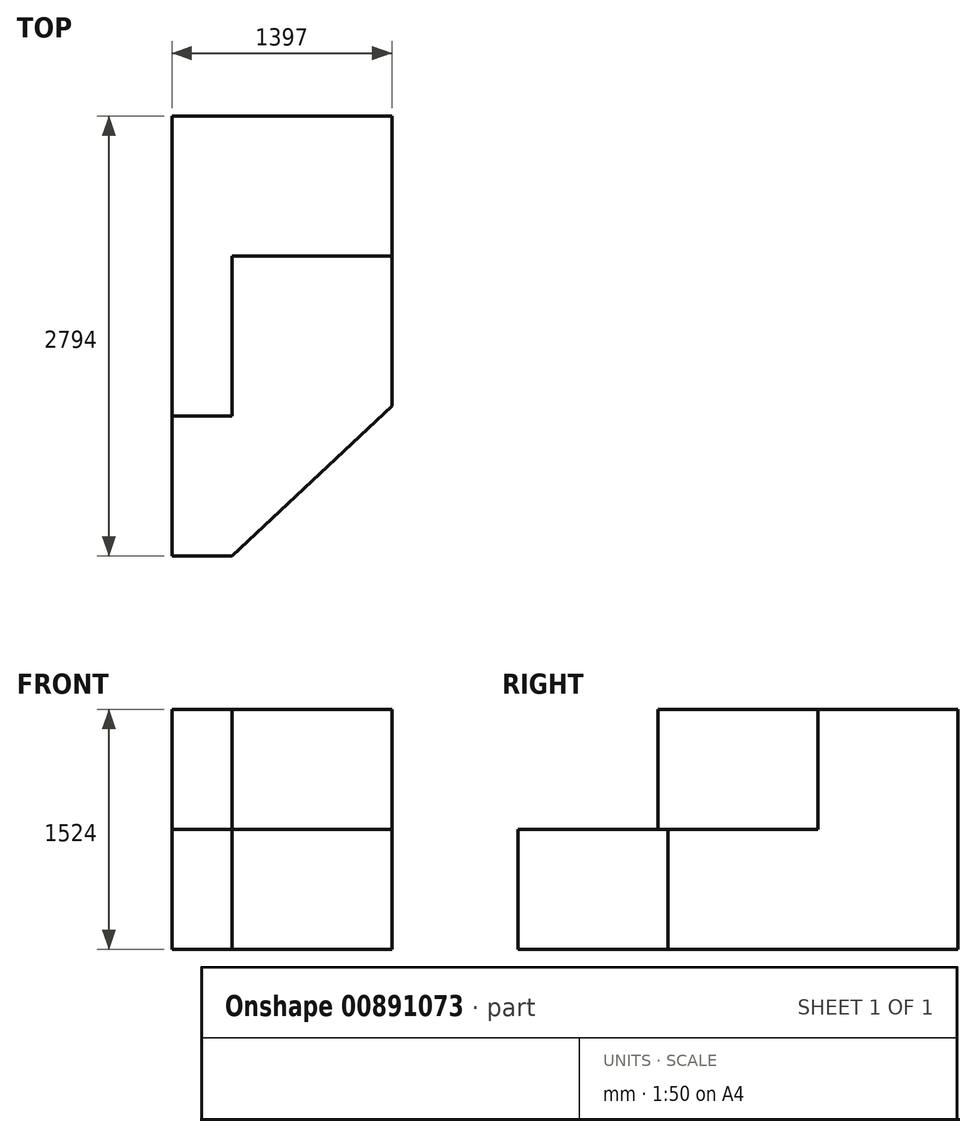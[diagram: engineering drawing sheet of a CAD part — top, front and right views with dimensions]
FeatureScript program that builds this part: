
annotation { "Feature Type Name" : "Feature", "Feature Type Description" : "" }
export const myFeature = defineFeature(function(context is Context, id is Id, definition is map)
    precondition{}
    {
        {
            var Q0;
            Q0=qCreatedBy(makeId("Right.planeOp"),FACE);
            var sketch = newSketch(context, id + "F0", { "sketchPlane" : qUnion([Q0])});
            skLineSegment(sketch, "E0.bottom", {"start": v(0, 0) * mm, "end": v(1778, 0) * mm});
            skLineSegment(sketch, "E0.top", {"start": v(0, -1524) * mm, "end": v(1778, -1524) * mm});
            skLineSegment(sketch, "E0.left", {"start": v(0, 0) * mm, "end": v(0, -1524) * mm});
            skLineSegment(sketch, "E0.right", {"start": v(1778, 0) * mm, "end": v(1778, -1524) * mm});
            skSolve(sketch);
        }
        {
            var Q0;
            Q0=makeQuery(id+"F0.imprint","IMPRINT",FACE,{"disambiguationData":[TD([[makeQuery(id+"F0.imprint","IMPRINT",EDGE,{"derivedFrom":sQuery(id+"F0.wireOp",EDGE,"E0.bottom")}),-1.0]])]});
            var sketch = newSketch(context, id + "F1", { "sketchPlane" : qUnion([Q0])});
            skLineSegment(sketch, "E1.bottom", {"start": v(0, 0) * mm, "end": v(889, 0) * mm});
            skLineSegment(sketch, "E1.top", {"start": v(0, -762) * mm, "end": v(889, -762) * mm});
            skLineSegment(sketch, "E1.left", {"start": v(0, 0) * mm, "end": v(0, -762) * mm});
            skLineSegment(sketch, "E1.right", {"start": v(889, 0) * mm, "end": v(889, -762) * mm});
            skSolve(sketch);
        }
        {
            var Q0;
            Q0=makeQuery(id+"F0.imprint","IMPRINT",FACE,{"disambiguationData":[TD([[makeQuery(id+"F0.imprint","IMPRINT",EDGE,{"derivedFrom":sQuery(id+"F0.wireOp",EDGE,"E0.bottom")}),-1.0]])]});
            extrude(context, id + "F2", {"entities" : qUnion([Q0]), "oppositeDirection" : true, "depth" : 1397 * mm, "offsetDistance" : 25.4 * mm});
        }
        {
            var Q0;
            Q0=makeQuery(id+"F1.imprint","IMPRINT",FACE,{"disambiguationData":[TD([[makeQuery(id+"F1.imprint","IMPRINT",EDGE,{"derivedFrom":sQuery(id+"F1.wireOp",EDGE,"E1.bottom")}),-1.0]])]});
            extrude(context, id + "F3", {"entities" : qUnion([Q0]), "operationType" : NewBodyOperationType.REMOVE, "oppositeDirection" : true, "depth" : 1755.14 * mm, "offsetDistance" : 25.4 * mm});
        }
        {
            var Q0;
            Q0=makeQuery(id+"F2.opExtrude","SWEPT_FACE",FACE,{"disambiguationData":[OSD([sQuery(id+"F0.wireOp",EDGE,"E0.left")])]});
            var sketch = newSketch(context, id + "F4", { "sketchPlane" : qUnion([Q0])});
            skLineSegment(sketch, "E2.bottom", {"start": v(-1397, -762) * mm, "end": v(0, -762) * mm});
            skLineSegment(sketch, "E2.top", {"start": v(-1397, -1524) * mm, "end": v(0, -1524) * mm});
            skLineSegment(sketch, "E2.left", {"start": v(-1397, -762) * mm, "end": v(-1397, -1524) * mm});
            skLineSegment(sketch, "E2.right", {"start": v(0, -762) * mm, "end": v(0, -1524) * mm});
            skSolve(sketch);
        }
        {
            var Q0;
            Q0=makeQuery(id+"F4.imprint","IMPRINT",FACE,{"disambiguationData":[TD([[makeQuery(id+"F4.imprint","IMPRINT",EDGE,{"derivedFrom":sQuery(id+"F4.wireOp",EDGE,"E2.bottom")}),-1.0]])]});
            extrude(context, id + "F5", {"entities" : qUnion([Q0]), "operationType" : NewBodyOperationType.ADD, "depth" : 1016 * mm, "offsetDistance" : 25.4 * mm});
        }
        {
            var Q0;
            Q0=makeQuery(id+"F5.boolean.opBoolean","MERGE",FACE,{"derivedFrom":[makeQuery(id+"F3.boolean.opBoolean","COPY",FACE,{"derivedFrom":makeQuery(id+"F3.opExtrude","SWEPT_FACE",FACE,{"disambiguationData":[OSD([sQuery(id+"F1.wireOp",EDGE,"E1.top")])]})}),makeQuery(id+"F5.opExtrude","SWEPT_FACE",FACE,{"disambiguationData":[OSD([sQuery(id+"F4.wireOp",EDGE,"E2.bottom")])]})]});
            var sketch = newSketch(context, id + "F6", { "sketchPlane" : qUnion([Q0])});
            skLineSegment(sketch, "E3", {"start": v(0, -63.5) * mm, "end": v(-1015.92, -1016) * mm});
            skSolve(sketch);
        }
        {
            var Q0;
            {var subQ0=sQuery(id+"F6.wireOp",EDGE,"E3");Q0=makeQuery(id+"F6.imprint","IMPRINT",FACE,{"disambiguationData":[TD([[makeQuery(id+"F6.imprint","IMPRINT",EDGE,{"derivedFrom":subQ0}),1.0]])]});}
            extrude(context, id + "F7", {"entities" : qUnion([Q0]), "operationType" : NewBodyOperationType.REMOVE, "oppositeDirection" : true, "depth" : 1226.82 * mm, "offsetDistance" : 25.4 * mm});
        }
        {
            var Q0;
            Q0=makeQuery(id+"F3.boolean.opBoolean","COPY",FACE,{"derivedFrom":makeQuery(id+"F3.opExtrude","SWEPT_FACE",FACE,{"disambiguationData":[OSD([sQuery(id+"F1.wireOp",EDGE,"E1.right")])]})});
            var sketch = newSketch(context, id + "F8", { "sketchPlane" : qUnion([Q0])});
            skLineSegment(sketch, "E4.bottom", {"start": v(-1397, -762) * mm, "end": v(-1016, -762) * mm});
            skLineSegment(sketch, "E4.top", {"start": v(-1397, 0) * mm, "end": v(-1016, 0) * mm});
            skLineSegment(sketch, "E4.left", {"start": v(-1397, -762) * mm, "end": v(-1397, 0) * mm});
            skLineSegment(sketch, "E4.right", {"start": v(-1016, -762) * mm, "end": v(-1016, 0) * mm});
            skSolve(sketch);
        }
        {
            var Q0;
            Q0=makeQuery(id+"F8.imprint","IMPRINT",FACE,{"disambiguationData":[TD([[makeQuery(id+"F8.imprint","IMPRINT",EDGE,{"derivedFrom":sQuery(id+"F8.wireOp",EDGE,"E4.bottom")}),1.0]])]});
            extrude(context, id + "F9", {"entities" : qUnion([Q0]), "operationType" : NewBodyOperationType.ADD, "depth" : 1016 * mm, "offsetDistance" : 25.4 * mm});
        }
    });
